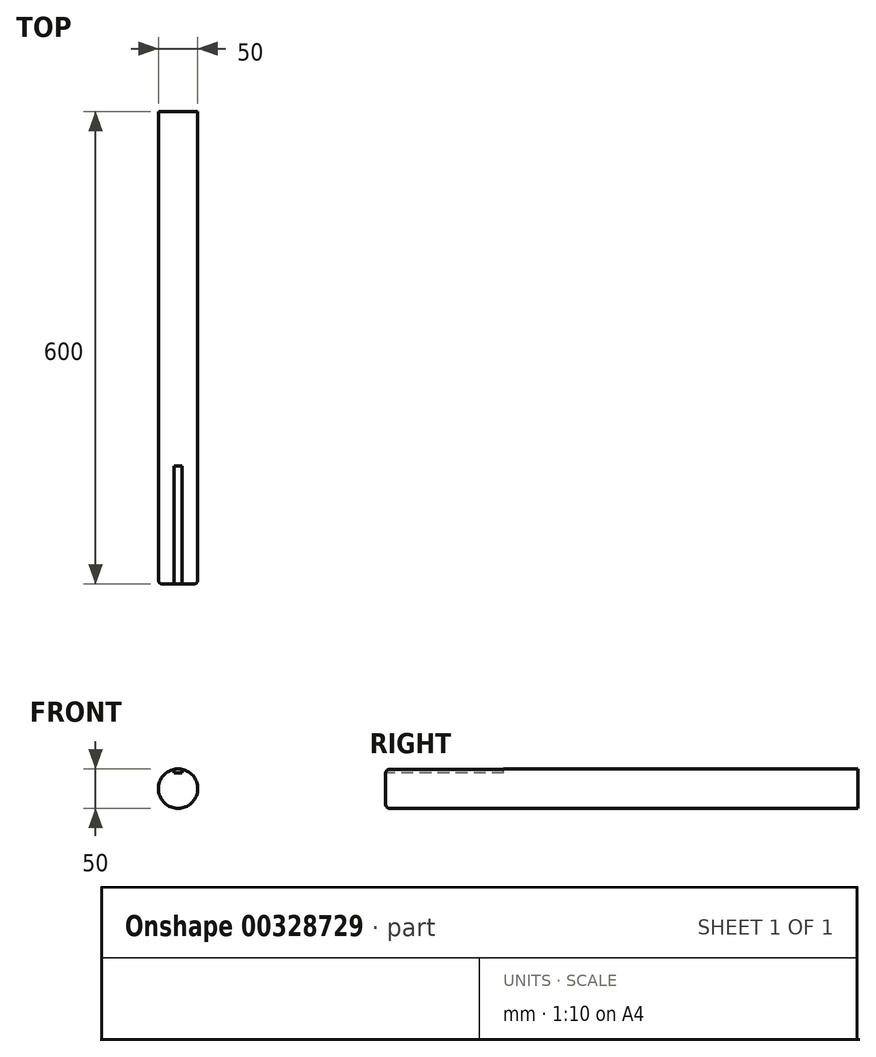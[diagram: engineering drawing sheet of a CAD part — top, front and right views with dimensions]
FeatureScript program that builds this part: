
annotation { "Feature Type Name" : "Feature", "Feature Type Description" : "" }
export const myFeature = defineFeature(function(context is Context, id is Id, definition is map)
    precondition{}
    {
        {
            var Q0;
            Q0=qCreatedBy(makeId("Front.planeOp"),FACE);
            var sketch = newSketch(context, id + "F0", { "sketchPlane" : qUnion([Q0])});
            skCircle(sketch, "E0", {"center": v(0, 0) * mm, "radius": 25 * mm});
            skLineSegment(sketch, "E1", {"start": v(0, 20) * mm, "end": v(-5, 20) * mm});
            skLineSegment(sketch, "E2", {"start": v(0, 20) * mm, "end": v(5, 20) * mm});
            skPoint(sketch, "E3.start.orphan", {"position": v(0, 25) * mm});
            skLineSegment(sketch, "E4", {"start": v(5, 20) * mm, "end": v(5, 24.5) * mm});
            skLineSegment(sketch, "E5", {"start": v(-5, 20) * mm, "end": v(-5, 24.5) * mm});
            skSolve(sketch);
        }
        {
            var Q0;
            Q0 = qSketchRegion(id + "F0", true);
            extrude(context, id + "F1", {"entities" : qUnion([Q0]), "depth" : 600 * mm});
        }
        {
            var Q0;
            Q0=makeQuery(id+"F1.opExtrude","CAP_FACE",FACE,{"disambiguationData":[OSD([sQuery(id+"F0.wireOp",EDGE,"E0")])],"isStart":false});
            var sketch = newSketch(context, id + "F2", { "sketchPlane" : qUnion([Q0])});
            skLineSegment(sketch, "E6", {"start": v(0, 20) * mm, "end": v(-5, 20) * mm});
            skLineSegment(sketch, "E7", {"start": v(0, 20) * mm, "end": v(5, 20) * mm});
            skLineSegment(sketch, "E8", {"start": v(-5, 20) * mm, "end": v(-5, 24.5) * mm});
            skLineSegment(sketch, "E9", {"start": v(5, 20) * mm, "end": v(5, 24.5) * mm});
            skPoint(sketch, "E10.start.orphan", {"position": v(0, 25) * mm});
            skSolve(sketch);
        }
        {
            var Q0;
            Q0 = qSketchRegion(id + "F2", true);
            var Q1;
            Q1=makeQuery(id+"F2.imprint","IMPRINT",FACE,{"disambiguationData":[TD([[makeQuery(id+"F2.imprint","IMPRINT",EDGE,{"derivedFrom":sQuery(id+"F2.wireOp",EDGE,"E6")}),-1.0]])]});
            extrude(context, id + "F3", {"entities" : qUnion([Q0, Q1]), "operationType" : NewBodyOperationType.REMOVE, "oppositeDirection" : true, "depth" : 150 * mm});
        }
        {
            var Q0;
            Q0=makeQuery(id+"F1.opExtrude","CAP_EDGE",EDGE,{"disambiguationData":[OSD([sQuery(id+"F0.wireOp",EDGE,"E0")])],"isStart":false});
            fillet(context, id + "F4", {"entities" : qUnion([Q0]), "radius" : 5 * mm, "tangentPropagation" : true, "allowEdgeOverflow" : false});
        }
    });
